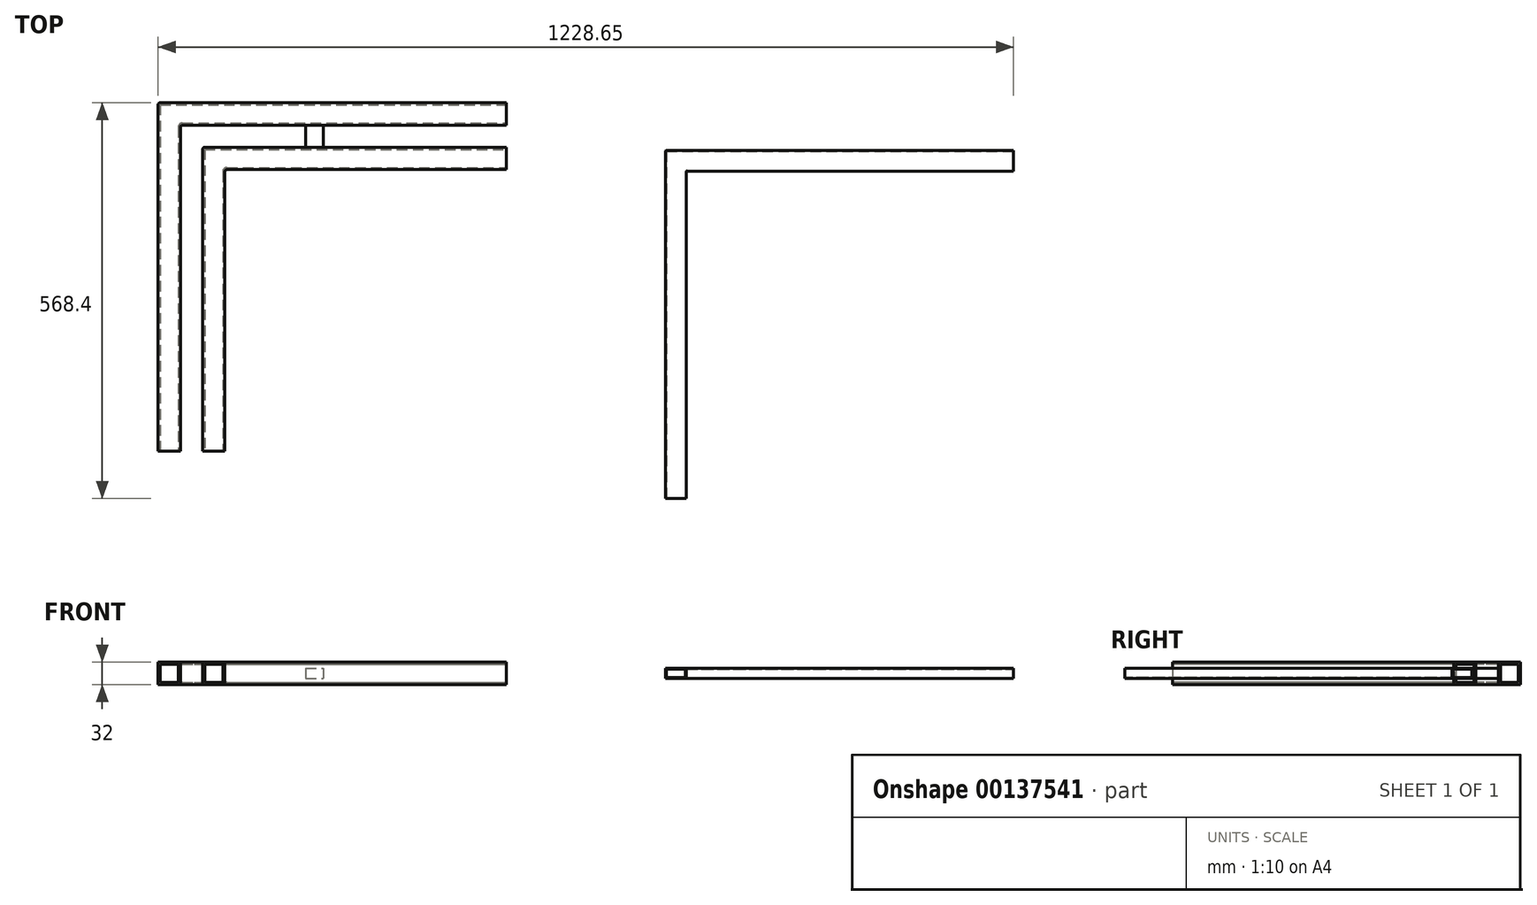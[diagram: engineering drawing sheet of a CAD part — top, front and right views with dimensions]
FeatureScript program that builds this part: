
annotation { "Feature Type Name" : "Feature", "Feature Type Description" : "" }
export const myFeature = defineFeature(function(context is Context, id is Id, definition is map)
    precondition{}
    {
        {
            var Q0;
            Q0=qCreatedBy(makeId("Top.planeOp"),FACE);
            var sketch = newSketch(context, id + "F0", { "sketchPlane" : qUnion([Q0])});
            skLineSegment(sketch, "E0.bottom", {"start": v(0, 0) * mm, "end": v(500, 0) * mm});
            skLineSegment(sketch, "E0.top", {"start": v(0, -500) * mm, "end": v(32, -500) * mm});
            skLineSegment(sketch, "E0.left", {"start": v(0, 0) * mm, "end": v(0, -500) * mm});
            skLineSegment(sketch, "E0.right", {"start": v(500, 0) * mm, "end": v(500, -32) * mm});
            skLineSegment(sketch, "E1.0", {"start": v(32, -32) * mm, "end": v(500, -32) * mm});
            skLineSegment(sketch, "E1.1", {"start": v(32, -32) * mm, "end": v(32, -500) * mm});
            skLineSegment(sketch, "E2.0", {"start": v(64, -64) * mm, "end": v(500, -64) * mm});
            skLineSegment(sketch, "E2.1", {"start": v(64, -64) * mm, "end": v(64, -500) * mm});
            skLineSegment(sketch, "E3.0", {"start": v(96, -96) * mm, "end": v(500, -96) * mm});
            skLineSegment(sketch, "E3.1", {"start": v(96, -96) * mm, "end": v(96, -500) * mm});
            skLineSegment(sketch, "E4.trimOffspring", {"start": v(500, -64) * mm, "end": v(500, -96) * mm});
            skLineSegment(sketch, "E5.trimOffspring", {"start": v(64, -500) * mm, "end": v(96, -500) * mm});
            skSolve(sketch);
        }
        {
            var Q0;
            Q0=makeQuery(id+"F0.imprint","IMPRINT",FACE,{"disambiguationData":[TD([[makeQuery(id+"F0.imprint","IMPRINT",EDGE,{"derivedFrom":sQuery(id+"F0.wireOp",EDGE,"E2.0")}),-1.0]])]});
            var Q1;
            Q1=makeQuery(id+"F0.imprint","IMPRINT",FACE,{"disambiguationData":[TD([[makeQuery(id+"F0.imprint","IMPRINT",EDGE,{"derivedFrom":sQuery(id+"F0.wireOp",EDGE,"E0.bottom")}),-1.0]])]});
            extrude(context, id + "F1", {"entities" : qUnion([Q0, Q1]), "depth" : 16 * mm, "hasSecondDirection" : true, "secondDirectionOppositeDirection" : true, "secondDirectionDepth" : 16 * mm});
        }
        {
            var Q0;
            Q0=makeQuery(id+"F1.opExtrude","SWEPT_EDGE",EDGE,{"disambiguationData":[OSD([sQuery(id+"F0.wireOp",EDGE,"E2.0"),sQuery(id+"F0.wireOp",EDGE,"E2.1")])]});
            var Q1;
            Q1=makeQuery(id+"F1.opExtrude","SWEPT_EDGE",EDGE,{"disambiguationData":[OSD([sQuery(id+"F0.wireOp",EDGE,"E0.bottom"),sQuery(id+"F0.wireOp",EDGE,"E0.left")])]});
            var Q2;
            Q2=makeQuery(id+"F1.opExtrude","SWEPT_EDGE",EDGE,{"disambiguationData":[OSD([sQuery(id+"F0.wireOp",EDGE,"E1.0"),sQuery(id+"F0.wireOp",EDGE,"E1.1")])]});
            var Q3;
            Q3=makeQuery(id+"F1.opExtrude","SWEPT_EDGE",EDGE,{"disambiguationData":[OSD([sQuery(id+"F0.wireOp",EDGE,"E3.0"),sQuery(id+"F0.wireOp",EDGE,"E3.1")])]});
            fillet(context, id + "F2", {"entities" : qUnion([Q0, Q1, Q2, Q3]), "radius" : 3 * mm, "tangentPropagation" : true, "allowEdgeOverflow" : false});
        }
        {
            var Q0;
            Q0=makeQuery(id+"F1.opExtrude","SWEPT_FACE",FACE,{"disambiguationData":[OSD([sQuery(id+"F0.wireOp",EDGE,"E0.right")])]});
            var Q1;
            Q1=makeQuery(id+"F1.opExtrude","SWEPT_FACE",FACE,{"disambiguationData":[OSD([sQuery(id+"F0.wireOp",EDGE,"E4.trimOffspring")])]});
            var Q2;
            Q2=makeQuery(id+"F1.opExtrude","SWEPT_FACE",FACE,{"disambiguationData":[OSD([sQuery(id+"F0.wireOp",EDGE,"E5.trimOffspring")])]});
            var Q3;
            Q3=makeQuery(id+"F1.opExtrude","SWEPT_FACE",FACE,{"disambiguationData":[OSD([sQuery(id+"F0.wireOp",EDGE,"E0.top")])]});
            shell(context, id + "F3", {"entities" : qUnion([Q0, Q1, Q2, Q3]), "thickness" : 3 * mm});
        }
        {
            var Q0;
            Q0=qCreatedBy(makeId("Top.planeOp"),FACE);
            var sketch = newSketch(context, id + "F4", { "sketchPlane" : qUnion([Q0])});
            skLineSegment(sketch, "E6.bottom", {"start": v(212.03, -32) * mm, "end": v(237.03, -32) * mm});
            skLineSegment(sketch, "E6.top", {"start": v(212.03, -64) * mm, "end": v(237.03, -64) * mm});
            skLineSegment(sketch, "E6.left", {"start": v(212.03, -32) * mm, "end": v(212.03, -64) * mm});
            skLineSegment(sketch, "E6.right", {"start": v(237.03, -32) * mm, "end": v(237.03, -64) * mm});
            skSolve(sketch);
        }
        {
            var Q0;
            Q0 = qSketchRegion(id + "F4", true);
            extrude(context, id + "F5", {"entities" : qUnion([Q0]), "depth" : 7.5 * mm, "hasSecondDirection" : true, "secondDirectionOppositeDirection" : true, "secondDirectionDepth" : 7.5 * mm});
        }
        {
            var Q0;
            Q0=qCreatedBy(makeId("Top.planeOp"),FACE);
            var sketch = newSketch(context, id + "F6", { "sketchPlane" : qUnion([Q0])});
            skLineSegment(sketch, "E7.bottom", {"start": v(728.65, -68.4) * mm, "end": v(1228.65, -68.4) * mm});
            skLineSegment(sketch, "E7.top", {"start": v(728.65, -568.4) * mm, "end": v(758.65, -568.4) * mm});
            skLineSegment(sketch, "E7.left", {"start": v(728.65, -68.4) * mm, "end": v(728.65, -568.4) * mm});
            skLineSegment(sketch, "E7.right", {"start": v(1228.65, -68.4) * mm, "end": v(1228.65, -98.4) * mm});
            skLineSegment(sketch, "E8.0", {"start": v(758.65, -98.4) * mm, "end": v(1228.65, -98.4) * mm});
            skLineSegment(sketch, "E8.1", {"start": v(758.65, -98.4) * mm, "end": v(758.65, -568.4) * mm});
            skSolve(sketch);
        }
        {
            var Q0;
            Q0=makeQuery(id+"F6.imprint","IMPRINT",FACE,{"disambiguationData":[TD([[makeQuery(id+"F6.imprint","IMPRINT",EDGE,{"derivedFrom":sQuery(id+"F6.wireOp",EDGE,"E7.bottom")}),-1.0]])]});
            extrude(context, id + "F7", {"entities" : qUnion([Q0]), "depth" : 7.5 * mm, "hasSecondDirection" : true, "secondDirectionOppositeDirection" : true, "secondDirectionDepth" : 7.5 * mm});
        }
        {
            var Q0;
            Q0=makeQuery(id+"F7.opExtrude","SWEPT_EDGE",EDGE,{"disambiguationData":[OSD([sQuery(id+"F6.wireOp",EDGE,"E7.bottom"),sQuery(id+"F6.wireOp",EDGE,"E7.left")])]});
            var Q1;
            Q1=makeQuery(id+"F7.opExtrude","SWEPT_EDGE",EDGE,{"disambiguationData":[OSD([sQuery(id+"F6.wireOp",EDGE,"E8.0"),sQuery(id+"F6.wireOp",EDGE,"E8.1")])]});
            fillet(context, id + "F8", {"entities" : qUnion([Q0, Q1]), "radius" : 1.5 * mm, "tangentPropagation" : true, "allowEdgeOverflow" : false});
        }
        {
            var Q0;
            Q0=makeQuery(id+"F7.opExtrude","SWEPT_FACE",FACE,{"disambiguationData":[OSD([sQuery(id+"F6.wireOp",EDGE,"E7.right")])]});
            var Q1;
            Q1=makeQuery(id+"F7.opExtrude","SWEPT_FACE",FACE,{"disambiguationData":[OSD([sQuery(id+"F6.wireOp",EDGE,"E7.top")])]});
            shell(context, id + "F9", {"entities" : qUnion([Q0, Q1]), "thickness" : 1.5 * mm});
        }
    });
